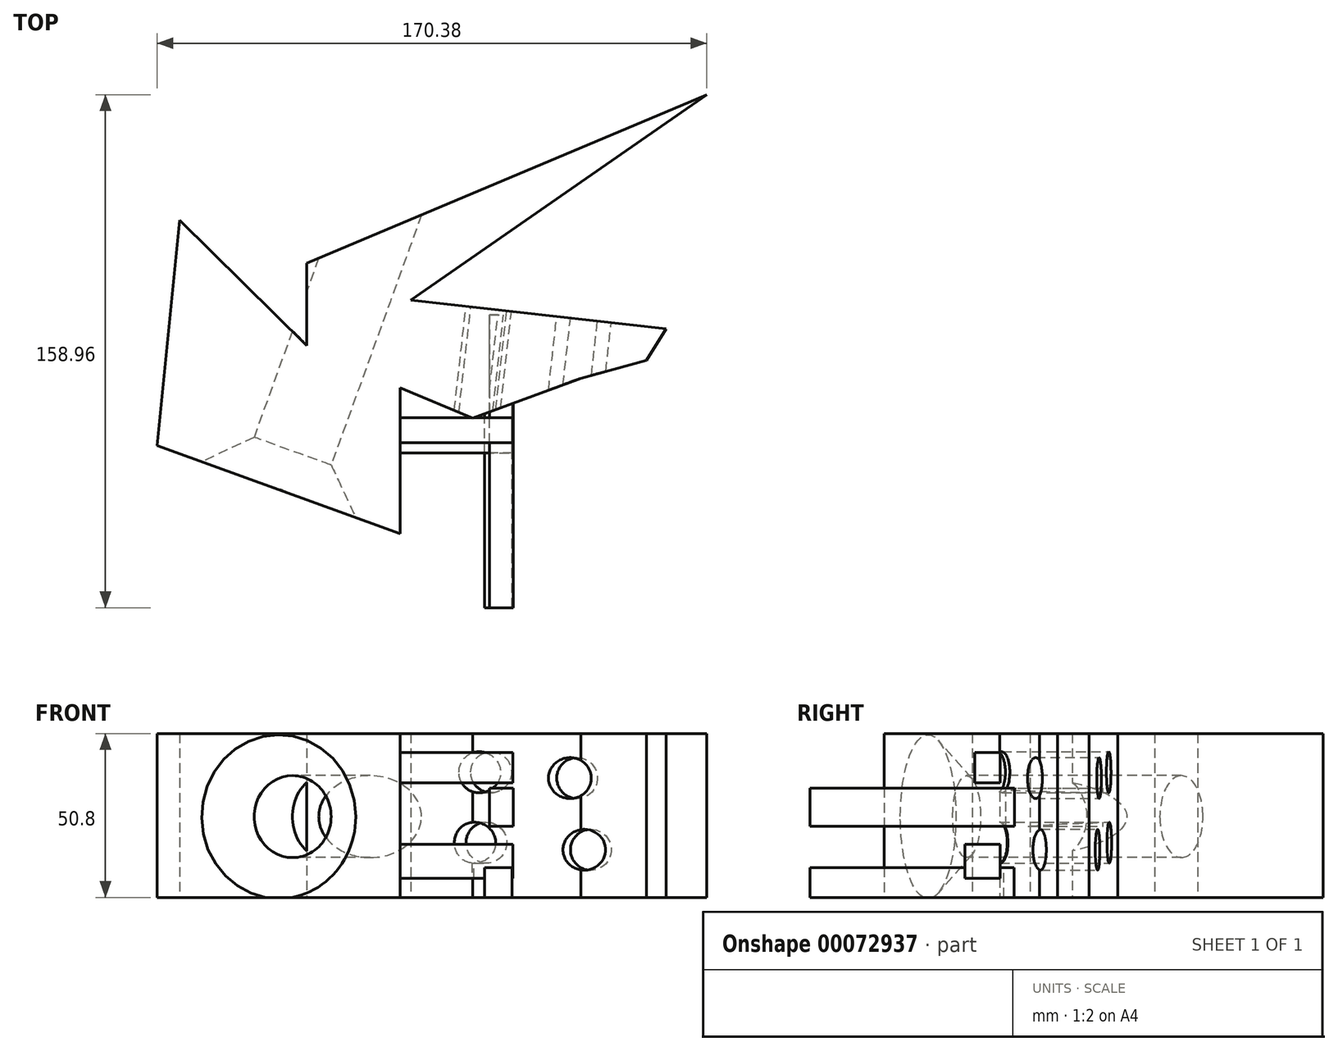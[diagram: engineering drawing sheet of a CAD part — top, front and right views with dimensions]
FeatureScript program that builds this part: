
annotation { "Feature Type Name" : "Feature", "Feature Type Description" : "" }
export const myFeature = defineFeature(function(context is Context, id is Id, definition is map)
    precondition{}
    {
        {
            var Q0;
            Q0=qCreatedBy(makeId("Top.planeOp"),FACE);
            var sketch = newSketch(context, id + "F0", { "sketchPlane" : qUnion([Q0])});
            skLineSegment(sketch, "E0", {"start": v(-63.27, 4.53) * mm, "end": v(15.9, -4.35) * mm});
            skLineSegment(sketch, "E1", {"start": v(9.8, -14.15) * mm, "end": v(-10.54, -19.7) * mm});
            skLineSegment(sketch, "E2", {"start": v(-44.03, -32.1) * mm, "end": v(-10.54, -19.7) * mm});
            skLineSegment(sketch, "E3", {"start": v(9.8, -14.15) * mm, "end": v(15.9, -4.35) * mm});
            skLineSegment(sketch, "E4", {"start": v(-63.27, 4.53) * mm, "end": v(28.49, 68.17) * mm});
            skLineSegment(sketch, "E5", {"start": v(28.49, 68.17) * mm, "end": v(-95.46, 16) * mm});
            skLineSegment(sketch, "E6", {"start": v(-95.46, -9.53) * mm, "end": v(-95.46, 16) * mm});
            skLineSegment(sketch, "E7", {"start": v(-95.46, -9.53) * mm, "end": v(-134.86, 29.32) * mm});
            skLineSegment(sketch, "E8", {"start": v(-134.86, 29.32) * mm, "end": v(-141.9, -40.6) * mm});
            skLineSegment(sketch, "E9", {"start": v(-141.9, -40.6) * mm, "end": v(-66.6, -67.8) * mm});
            skLineSegment(sketch, "E10", {"start": v(-66.6, -67.8) * mm, "end": v(-66.6, -22.66) * mm});
            skLineSegment(sketch, "E11", {"start": v(-66.6, -22.66) * mm, "end": v(-44.03, -32.1) * mm});
            skSolve(sketch);
        }
        {
            var Q0;
            Q0=makeQuery(id+"F0.imprint","IMPRINT",FACE,{"disambiguationData":[TD([[makeQuery(id+"F0.imprint","IMPRINT",EDGE,{"derivedFrom":sQuery(id+"F0.wireOp",EDGE,"E0")}),-1.0]])]});
            extrude(context, id + "F1", {"entities" : qUnion([Q0]), "depth" : 50.8 * mm});
        }
        {
            var Q0;
            Q0=makeQuery(id+"F1.opExtrude","SWEPT_FACE",FACE,{"disambiguationData":[OSD([sQuery(id+"F0.wireOp",EDGE,"E9")])]});
            var sketch = newSketch(context, id + "F2", { "sketchPlane" : qUnion([Q0])});
            skPoint(sketch, "E12", {"position": v(-79.58, 25.03) * mm});
            skSolve(sketch);
        }
        {
            var Q0;
            Q0=sQuery(id+"F2.wireOp",VERTEX,"E12");
            var Q1;
            Q1=makeQuery(id+"F1.opExtrude","SWEPT_BODY",BODY,{"disambiguationData":[OSD([sQuery(id+"F0.wireOp",EDGE,"E0"),sQuery(id+"F0.wireOp",EDGE,"E1"),sQuery(id+"F0.wireOp",EDGE,"E2"),sQuery(id+"F0.wireOp",EDGE,"E3"),sQuery(id+"F0.wireOp",EDGE,"E4"),sQuery(id+"F0.wireOp",EDGE,"E5"),sQuery(id+"F0.wireOp",EDGE,"E6"),sQuery(id+"F0.wireOp",EDGE,"E7"),sQuery(id+"F0.wireOp",EDGE,"E8"),sQuery(id+"F0.wireOp",EDGE,"E9"),sQuery(id+"F0.wireOp",EDGE,"E10"),sQuery(id+"F0.wireOp",EDGE,"E11")])]});
            hole(context, id + "F3", {"style" : HoleStyle.C_SINK, "holeDiameter" : 25.4 * mm, "cSinkDiameter" : 50.8 * mm, "endStyle" : HoleEndStyle.THROUGH, "locations" : qUnion([Q0]), "scope" : qUnion([Q1]), "cSinkAngle" : 90 * degree});
        }
        {
            var Q0;
            Q0=makeQuery(id+"F1.opExtrude","SWEPT_FACE",FACE,{"disambiguationData":[OSD([sQuery(id+"F0.wireOp",EDGE,"E0")])]});
            var sketch = newSketch(context, id + "F4", { "sketchPlane" : qUnion([Q0])});
            skLineSegment(sketch, "E13", {"start": v(7.24, 14.76) * mm, "end": v(39.8, 16.96) * mm});
            skLineSegment(sketch, "E14", {"start": v(39.8, 16.96) * mm, "end": v(38.32, 38.8) * mm});
            skLineSegment(sketch, "E15", {"start": v(38.32, 38.8) * mm, "end": v(11.51, 36.98) * mm});
            skLineSegment(sketch, "E16", {"start": v(11.51, 36.98) * mm, "end": v(7.24, 14.76) * mm});
            skSolve(sketch);
        }
        {
            var Q0;
            Q0=sQuery(id+"F4.wireOp",VERTEX,"E13.start");
            var Q1;
            Q1=sQuery(id+"F4.wireOp",VERTEX,"E16.start");
            var Q2;
            Q2=sQuery(id+"F4.wireOp",VERTEX,"E15.start");
            var Q3;
            Q3=sQuery(id+"F4.wireOp",VERTEX,"E14.start");
            var Q4;
            Q4=makeQuery(id+"F1.opExtrude","SWEPT_BODY",BODY,{"disambiguationData":[OSD([sQuery(id+"F0.wireOp",EDGE,"E0"),sQuery(id+"F0.wireOp",EDGE,"E1"),sQuery(id+"F0.wireOp",EDGE,"E2"),sQuery(id+"F0.wireOp",EDGE,"E3"),sQuery(id+"F0.wireOp",EDGE,"E4"),sQuery(id+"F0.wireOp",EDGE,"E5"),sQuery(id+"F0.wireOp",EDGE,"E6"),sQuery(id+"F0.wireOp",EDGE,"E7"),sQuery(id+"F0.wireOp",EDGE,"E8"),sQuery(id+"F0.wireOp",EDGE,"E9"),sQuery(id+"F0.wireOp",EDGE,"E10"),sQuery(id+"F0.wireOp",EDGE,"E11")])]});
            hole(context, id + "F5", {"style" : HoleStyle.C_SINK, "holeDiameter" : 12.7 * mm, "cSinkDiameter" : 12.7 * mm, "endStyle" : HoleEndStyle.THROUGH, "locations" : qUnion([Q0, Q1, Q2, Q3]), "scope" : qUnion([Q4]), "cSinkAngle" : 90 * degree});
        }
        {
            var Q0;
            Q0=qCreatedBy(makeId("Front.planeOp"),FACE);
            var sketch = newSketch(context, id + "F6", { "sketchPlane" : qUnion([Q0])});
            skLineSegment(sketch, "E17.bottom", {"start": v(-40.42, 0) * mm, "end": v(-31.92, 0) * mm});
            skLineSegment(sketch, "E17.top", {"start": v(-40.42, 9.25) * mm, "end": v(-31.92, 9.25) * mm});
            skLineSegment(sketch, "E17.left", {"start": v(-40.42, 0) * mm, "end": v(-40.42, 9.25) * mm});
            skLineSegment(sketch, "E17.right", {"start": v(-31.92, 0) * mm, "end": v(-31.92, 9.25) * mm});
            skLineSegment(sketch, "E18.bottom", {"start": v(-38.86, 22.07) * mm, "end": v(-31.47, 22.07) * mm});
            skLineSegment(sketch, "E18.top", {"start": v(-38.86, 33.88) * mm, "end": v(-31.47, 33.88) * mm});
            skLineSegment(sketch, "E18.left", {"start": v(-38.86, 22.07) * mm, "end": v(-38.86, 33.88) * mm});
            skLineSegment(sketch, "E18.right", {"start": v(-31.47, 22.07) * mm, "end": v(-31.47, 33.88) * mm});
            skSolve(sketch);
        }
        {
            var Q0;
            Q0 = qSketchRegion(id + "F6", true);
            extrude(context, id + "F7", {"entities" : qUnion([Q0]), "operationType" : NewBodyOperationType.ADD, "depth" : 90.8 * mm});
        }
        {
            var Q0;
            Q0=makeQuery(id+"F1.opExtrude","SWEPT_FACE",FACE,{"disambiguationData":[OSD([sQuery(id+"F0.wireOp",EDGE,"E10")])]});
            var sketch = newSketch(context, id + "F8", { "sketchPlane" : qUnion([Q0])});
            skLineSegment(sketch, "E19.bottom", {"start": v(-42.87, 5.95) * mm, "end": v(-31.95, 5.95) * mm});
            skLineSegment(sketch, "E19.top", {"start": v(-42.87, 16.44) * mm, "end": v(-31.95, 16.44) * mm});
            skLineSegment(sketch, "E19.left", {"start": v(-42.87, 5.95) * mm, "end": v(-42.87, 16.44) * mm});
            skLineSegment(sketch, "E19.right", {"start": v(-31.95, 5.95) * mm, "end": v(-31.95, 16.44) * mm});
            skLineSegment(sketch, "E20.bottom", {"start": v(-39.72, 35.5) * mm, "end": v(-31.95, 35.5) * mm});
            skLineSegment(sketch, "E20.top", {"start": v(-39.72, 44.87) * mm, "end": v(-31.95, 44.87) * mm});
            skLineSegment(sketch, "E20.left", {"start": v(-39.72, 35.5) * mm, "end": v(-39.72, 44.87) * mm});
            skLineSegment(sketch, "E20.right", {"start": v(-31.95, 35.5) * mm, "end": v(-31.95, 44.87) * mm});
            skSolve(sketch);
        }
        {
            var Q0;
            Q0 = qSketchRegion(id + "F8", true);
            extrude(context, id + "F9", {"entities" : qUnion([Q0]), "operationType" : NewBodyOperationType.ADD, "depth" : 34.95 * mm});
        }
    });
